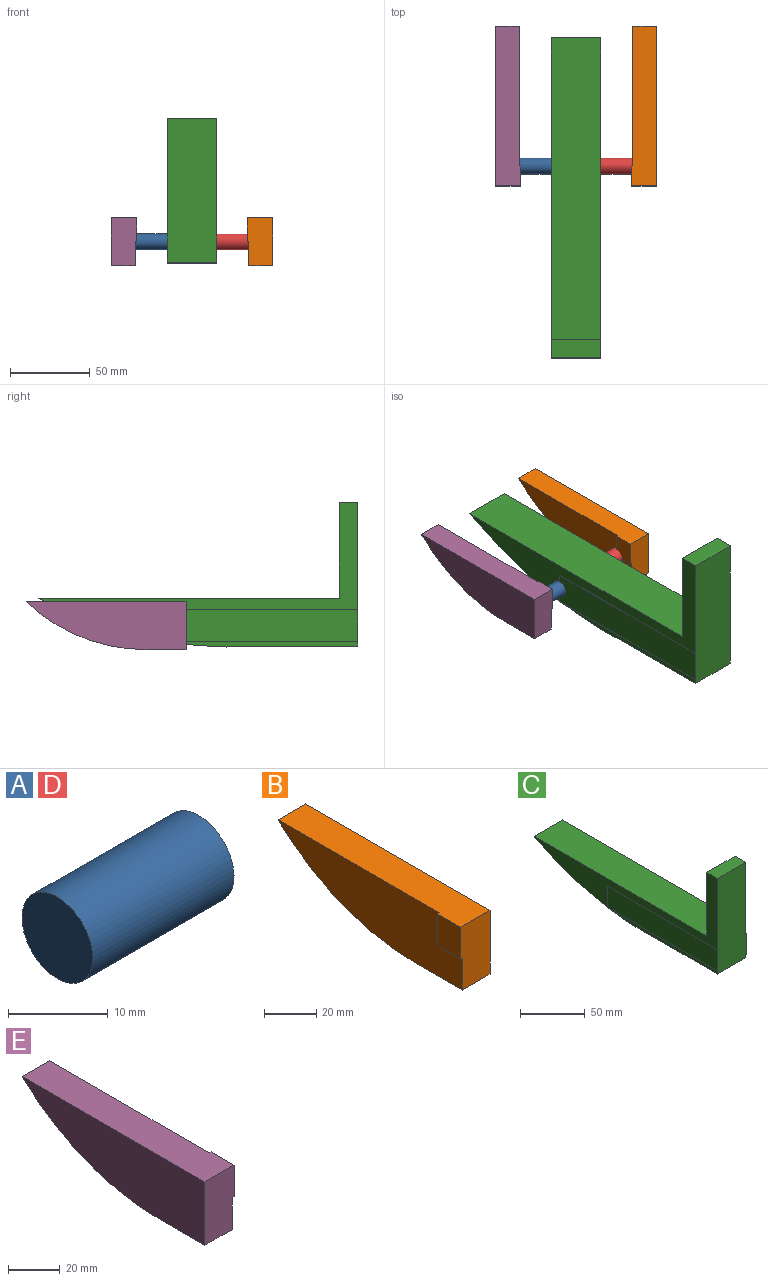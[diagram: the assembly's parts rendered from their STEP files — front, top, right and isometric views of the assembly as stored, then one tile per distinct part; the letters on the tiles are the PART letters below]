
ASSEMBLY  parts=5 mates=9
PART A: 3 faces, bbox 20x10x10 mm
  f0: cylinder r=5mm len=20mm, axis (-1,0,0), area 628.3mm2, adj f1,f2
  f1: plane 10x10mm, normal (1,0,0), area 78.5mm2, adj f0
  f2: plane 10x10mm, normal (-1,0,0), area 78.5mm2, adj f0
PART B: 9 faces, bbox 16x100x30 mm
  f0: plane 100x16mm, normal (0,0,1), area 1512.5mm2, adj f1,f3,f4,f5,f7,f8
  f1: plane 30x16mm, normal (0,-1,0), area 465mm2, adj f0,f2,f4,f5,f6,f8
  f2: plane 25x15mm, normal (0,0,-1), area 375mm2, adj f1,f3,f4,f5
  f3: cylinder r=108.75mm len=75mm, axis (-1,0,0), area 1241.4mm2, adj f0,f2,f4,f5
  f4: plane 100x30mm, normal (1,0,0), area 2297mm2, adj f0,f1,f2,f3
  f5: plane 100x30mm, normal (-1,0,0), area 2109.5mm2, adj f0,f1,f2,f3,f6,f7
  f6: plane 12.5x1mm, normal (0,0,-1), area 12.5mm2, adj f1,f5,f7,f8
  f7: plane 15x1mm, normal (0,1,0), area 15mm2, adj f0,f5,f6,f8
  f8: plane 15x12.5mm, normal (-1,0,0), area 187.5mm2, adj f0,f1,f6,f7
PART C: 18 faces, bbox 31.2x200x90.4 mm
  f0: plane 120x3.39mm, normal (-1,0,0), area 329.6mm2, adj f4,f5,f7,f15
  f1: plane 120x0.2mm, normal (0,0,1), area 24mm2, adj f3,f7,f11,f12
  f2: plane 120x0.2mm, normal (0,0,-1), area 24mm2, adj f3,f7,f11,f13
  f3: plane 20x0.2mm, normal (0,1,0), area 4mm2, adj f1,f2,f11,f12
  f4: plane 63.17x30.8mm, normal (0,0,-1), area 1945.6mm2, adj f0,f5,f7,f13
  f5: cylinder r=258.63mm len=136.83mm, axis (-1,0,0), area 4369mm2, adj f0,f4,f6,f8,f12,f13
  f6: plane 188.29x30.8mm, normal (0,0,1), area 5799.3mm2, adj f5,f8,f9,f12
  f7: plane 90x31.2mm, normal (0,-1,0), area 2780mm2, adj f0,f1,f2,f4,f8,f10,f11,f12
  f8: plane 200x87.05mm, normal (-1,0,0), area 2826.6mm2, adj f5,f6,f7,f9,f10,f14,f16
  f9: plane 60x30.8mm, normal (0,1,0), area 1848mm2, adj f6,f8,f10,f12
  f10: plane 30.8x11.71mm, normal (0,0,1), area 360.7mm2, adj f7,f8,f9,f12
  f11: plane 120x20mm, normal (1,0,0), area 2400mm2, adj f1,f2,f3,f7
  f12: plane 200x87.05mm, normal (1,0,0), area 2826.6mm2, adj f1,f3,f5,f6,f7,f9,f10
  f13: plane 120x3.39mm, normal (1,0,0), area 329.6mm2, adj f2,f4,f5,f7
  f14: plane 120x0.2mm, normal (0,0,1), area 24mm2, adj f7,f8,f16,f17
  f15: plane 120x0.2mm, normal (0,0,-1), area 24mm2, adj f0,f7,f16,f17
  f16: plane 20x0.2mm, normal (0,1,0), area 4mm2, adj f8,f14,f15,f17
  f17: plane 120x20mm, normal (-1,0,0), area 2400mm2, adj f7,f14,f15,f16
PART D: same geometry as A
PART E: 9 faces, bbox 16x100x30 mm
  f0: plane 100x16mm, normal (0,0,1), area 1512.5mm2, adj f1,f3,f4,f5,f7,f8
  f1: plane 30x16mm, normal (0,-1,0), area 465mm2, adj f0,f2,f4,f5,f6,f8
  f2: plane 25x15mm, normal (0,0,-1), area 375mm2, adj f1,f3,f4,f5
  f3: cylinder r=108.75mm len=75mm, axis (1,0,0), area 1241.4mm2, adj f0,f2,f4,f5
  f4: plane 100x30mm, normal (-1,0,0), area 2297mm2, adj f0,f1,f2,f3
  f5: plane 100x30mm, normal (1,0,0), area 2109.5mm2, adj f0,f1,f2,f3,f6,f7
  f6: plane 12.5x1mm, normal (0,0,-1), area 12.5mm2, adj f1,f5,f7,f8
  f7: plane 15x1mm, normal (0,1,0), area 15mm2, adj f0,f5,f6,f8
  f8: plane 15x12.5mm, normal (1,0,0), area 187.5mm2, adj f0,f1,f6,f7
PLACE A rot(axis=(0,0.71,0.71),180deg) t=(-22.74,-68.19,-112.95)mm
PLACE B t=(28.06,-30.69,-112.95)mm
PLACE C t=(-22.74,-88.19,-110.9)mm
PLACE D t=(8.06,-68.19,-112.95)mm
PLACE E t=(77.26,-30.69,-112.95)mm
MATE parallel A.f0 <-> E.f5  axis (-1,0,0) through (-42.74,-68.19,-112.95)mm
MATE parallel C.f8 <-> A.f0  axis (-1,0,0) through (-22.74,-68.19,-112.95)mm
MATE parallel A.f0 <-> E.f5  axis (-1,0,0) through (-42.74,-68.19,-112.95)mm
MATE parallel A.f0 <-> C.f8  axis (1,0,0) through (-22.74,-68.19,-112.95)mm
MATE parallel D.f0 <-> B.f5  axis (1,0,0) through (28.06,-68.19,-112.95)mm
MATE parallel D.f0 <-> C.f12  axis (-1,0,0) through (8.06,-68.19,-112.95)mm
MATE parallel B.f5 <-> D.f0  axis (-1,0,0) through (28.06,-68.19,-112.95)mm
MATE parallel D.f0 <-> C.f12  axis (-1,0,0) through (8.06,-68.19,-112.95)mm
MATE parallel B.f5 <-> D.f0  axis (-1,0,0) through (28.06,-68.19,-112.95)mm
